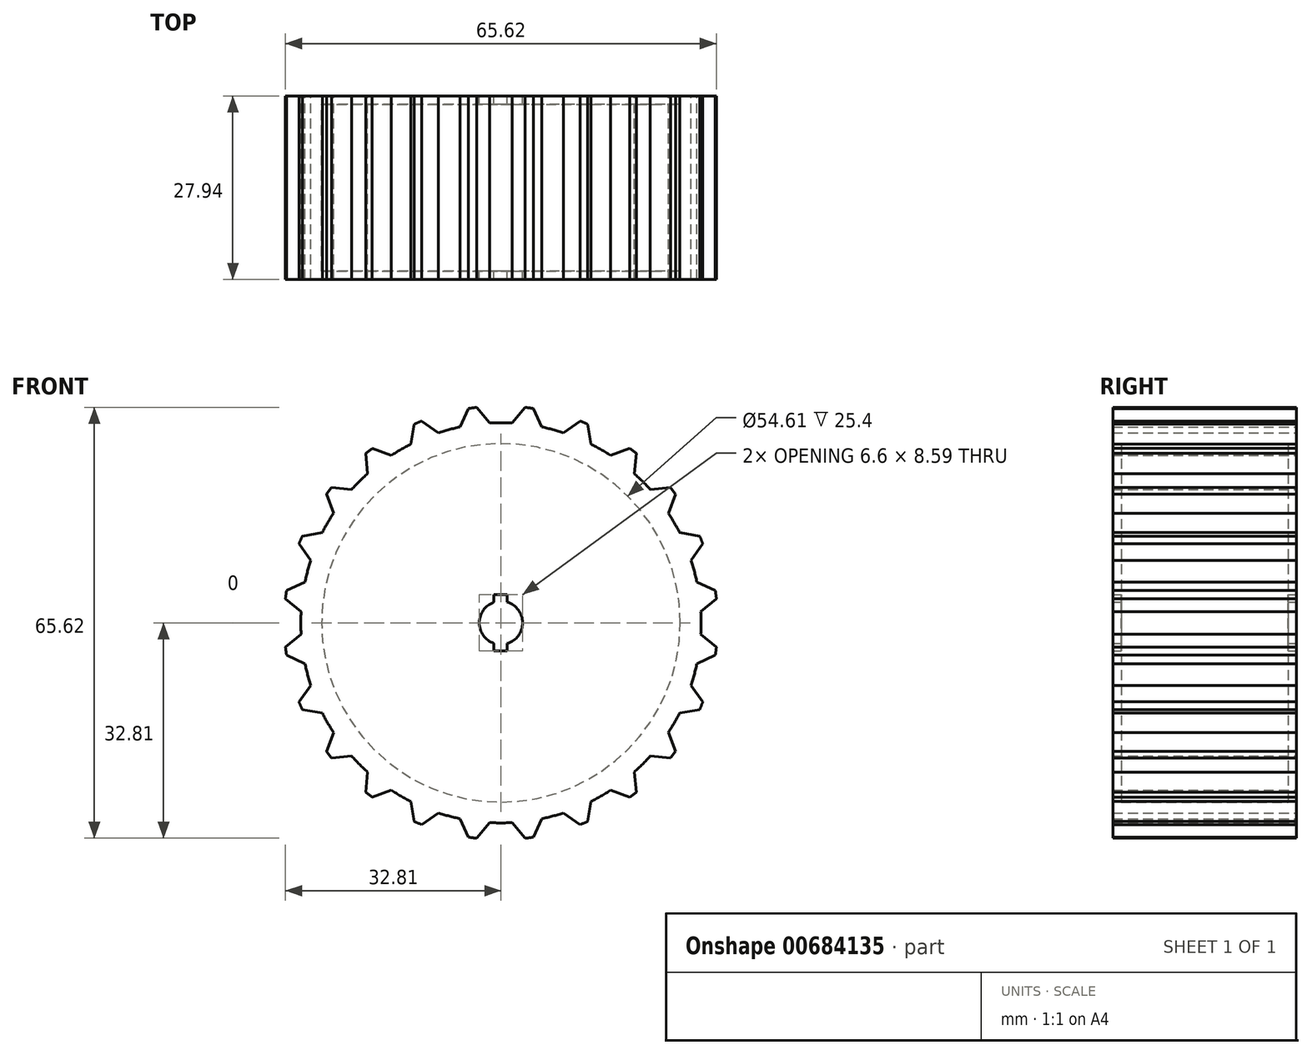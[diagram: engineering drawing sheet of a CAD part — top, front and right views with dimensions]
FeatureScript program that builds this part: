
annotation { "Feature Type Name" : "Feature", "Feature Type Description" : "" }
export const myFeature = defineFeature(function(context is Context, id is Id, definition is map)
    precondition{}
    {
        {
            var Q0;
            Q0=qCreatedBy(makeId("Front.planeOp"),FACE);
            var sketch = newSketch(context, id + "F0", { "sketchPlane" : qUnion([Q0])});
            skCircle(sketch, "E0", {"center": v(0, 0) * mm, "radius": 30.48 * mm});
            skCircle(sketch, "E1", {"center": v(0, 0) * mm, "radius": 33.02 * mm});
            skCircle(sketch, "E2.0", {"center": v(0, 0) * mm, "radius": 3.3 * mm});
            skLineSegment(sketch, "E3", {"start": v(-0.04, 5.09) * mm, "end": v(-0.04, -3.3) * mm, "construction": true});
            skLineSegment(sketch, "E4", {"start": v(-1.06, 3.13) * mm, "end": v(-1.06, 4.3) * mm});
            skLineSegment(sketch, "E5", {"start": v(-1.06, 4.3) * mm, "end": v(0.98, 4.3) * mm});
            skLineSegment(sketch, "E6", {"start": v(0.98, 4.3) * mm, "end": v(0.98, 3.15) * mm});
            skPoint(sketch, "E7", {"position": v(-0.04, 4.3) * mm});
            skLineSegment(sketch, "E8", {"start": v(0, 0) * mm, "end": v(-3.9, 0) * mm, "construction": true});
            skPoint(sketch, "E9.MirrorP", {"position": v(-0.04, -4.3) * mm});
            skLineSegment(sketch, "E10.MirrorCS", {"start": v(-1.06, -4.3) * mm, "end": v(0.98, -4.3) * mm});
            skLineSegment(sketch, "E11.MirrorCS", {"start": v(-1.06, -3.13) * mm, "end": v(-1.06, -4.3) * mm});
            skLineSegment(sketch, "E12.MirrorCS", {"start": v(0.98, -4.3) * mm, "end": v(0.98, -3.15) * mm});
            skSolve(sketch);
        }
        {
            var Q0;
            Q0 = qSketchRegion(id + "F0", true);
            extrude(context, id + "F1", {"entities" : qUnion([Q0]), "depth" : 27.94 * mm, "offsetDistance" : 25.4 * mm});
        }
        {
            var Q0;
            Q0=qCreatedBy(makeId("Front.planeOp"),FACE);
            var sketch = newSketch(context, id + "F2", { "sketchPlane" : qUnion([Q0])});
            skLineSegment(sketch, "E13", {"start": v(0, 44.27) * mm, "end": v(0, -42.94) * mm, "construction": true});
            skPoint(sketch, "E14", {"position": v(0, 33.02) * mm});
            skPoint(sketch, "E15", {"position": v(0, 30.48) * mm});
            skLineSegment(sketch, "E16", {"start": v(-1.71, 30.43) * mm, "end": v(-3.68, 32.81) * mm});
            skLineSegment(sketch, "E17", {"start": v(1.71, 30.43) * mm, "end": v(3.68, 32.81) * mm});
            skArc(sketch, "E18", {"start": v(3.68, 32.81) * mm, "mid": v(0, 33.02) * mm, "end": v(-3.68, 32.81) * mm});
            skArc(sketch, "E19", {"start": v(1.71, 30.43) * mm, "mid": v(0, 30.48) * mm, "end": v(-1.71, 30.43) * mm});
            skLineSegment(sketch, "E20.1.0", {"start": v(-6.22, 29.84) * mm, "end": v(-4.94, 32.65) * mm});
            skLineSegment(sketch, "E20.1.1", {"start": v(-9.53, 28.95) * mm, "end": v(-12.05, 30.74) * mm});
            skArc(sketch, "E20.1.2", {"start": v(-4.94, 32.65) * mm, "mid": v(-8.55, 31.9) * mm, "end": v(-12.05, 30.74) * mm});
            skArc(sketch, "E20.1.3", {"start": v(-6.22, 29.84) * mm, "mid": v(-7.89, 29.44) * mm, "end": v(-9.53, 28.95) * mm});
            skLineSegment(sketch, "E20.2.0", {"start": v(-13.73, 27.21) * mm, "end": v(-13.22, 30.26) * mm});
            skLineSegment(sketch, "E20.2.1", {"start": v(-16.7, 25.5) * mm, "end": v(-19.6, 26.58) * mm});
            skArc(sketch, "E20.2.2", {"start": v(-13.22, 30.26) * mm, "mid": v(-16.51, 28.6) * mm, "end": v(-19.6, 26.58) * mm});
            skArc(sketch, "E20.2.3", {"start": v(-13.73, 27.21) * mm, "mid": v(-15.24, 26.4) * mm, "end": v(-16.7, 25.5) * mm});
            skLineSegment(sketch, "E20.3.0", {"start": v(-20.3, 22.73) * mm, "end": v(-20.6, 25.8) * mm});
            skLineSegment(sketch, "E20.3.1", {"start": v(-22.73, 20.3) * mm, "end": v(-25.8, 20.6) * mm});
            skArc(sketch, "E20.3.2", {"start": v(-20.6, 25.8) * mm, "mid": v(-23.35, 23.35) * mm, "end": v(-25.8, 20.6) * mm});
            skArc(sketch, "E20.3.3", {"start": v(-20.3, 22.73) * mm, "mid": v(-21.55, 21.55) * mm, "end": v(-22.73, 20.3) * mm});
            skLineSegment(sketch, "E20.4.0", {"start": v(-25.5, 16.7) * mm, "end": v(-26.58, 19.6) * mm});
            skLineSegment(sketch, "E20.4.1", {"start": v(-27.21, 13.73) * mm, "end": v(-30.26, 13.22) * mm});
            skArc(sketch, "E20.4.2", {"start": v(-26.58, 19.6) * mm, "mid": v(-28.6, 16.5) * mm, "end": v(-30.26, 13.22) * mm});
            skArc(sketch, "E20.4.3", {"start": v(-25.5, 16.7) * mm, "mid": v(-26.4, 15.24) * mm, "end": v(-27.21, 13.73) * mm});
            skLineSegment(sketch, "E20.5.0", {"start": v(-28.95, 9.53) * mm, "end": v(-30.74, 12.05) * mm});
            skLineSegment(sketch, "E20.5.1", {"start": v(-29.84, 6.22) * mm, "end": v(-32.65, 4.94) * mm});
            skArc(sketch, "E20.5.2", {"start": v(-30.74, 12.05) * mm, "mid": v(-31.9, 8.55) * mm, "end": v(-32.65, 4.94) * mm});
            skArc(sketch, "E20.5.3", {"start": v(-28.95, 9.53) * mm, "mid": v(-29.44, 7.89) * mm, "end": v(-29.84, 6.22) * mm});
            skLineSegment(sketch, "E20.6.0", {"start": v(-30.43, 1.71) * mm, "end": v(-32.81, 3.68) * mm});
            skLineSegment(sketch, "E20.6.1", {"start": v(-30.43, -1.71) * mm, "end": v(-32.81, -3.68) * mm});
            skArc(sketch, "E20.6.2", {"start": v(-32.81, 3.68) * mm, "mid": v(-33.02, 0) * mm, "end": v(-32.81, -3.68) * mm});
            skArc(sketch, "E20.6.3", {"start": v(-30.43, 1.71) * mm, "mid": v(-30.48, 0) * mm, "end": v(-30.43, -1.71) * mm});
            skLineSegment(sketch, "E20.7.0", {"start": v(-29.84, -6.22) * mm, "end": v(-32.65, -4.94) * mm});
            skLineSegment(sketch, "E20.7.1", {"start": v(-28.95, -9.53) * mm, "end": v(-30.74, -12.05) * mm});
            skArc(sketch, "E20.7.2", {"start": v(-32.65, -4.94) * mm, "mid": v(-31.9, -8.55) * mm, "end": v(-30.74, -12.05) * mm});
            skArc(sketch, "E20.7.3", {"start": v(-29.84, -6.22) * mm, "mid": v(-29.44, -7.89) * mm, "end": v(-28.95, -9.53) * mm});
            skLineSegment(sketch, "E20.8.0", {"start": v(-27.21, -13.73) * mm, "end": v(-30.26, -13.22) * mm});
            skLineSegment(sketch, "E20.8.1", {"start": v(-25.5, -16.7) * mm, "end": v(-26.58, -19.6) * mm});
            skArc(sketch, "E20.8.2", {"start": v(-30.26, -13.22) * mm, "mid": v(-28.6, -16.5) * mm, "end": v(-26.58, -19.6) * mm});
            skArc(sketch, "E20.8.3", {"start": v(-27.21, -13.73) * mm, "mid": v(-26.4, -15.24) * mm, "end": v(-25.5, -16.7) * mm});
            skLineSegment(sketch, "E20.9.0", {"start": v(-22.73, -20.3) * mm, "end": v(-25.8, -20.6) * mm});
            skLineSegment(sketch, "E20.9.1", {"start": v(-20.3, -22.73) * mm, "end": v(-20.6, -25.8) * mm});
            skArc(sketch, "E20.9.2", {"start": v(-25.8, -20.6) * mm, "mid": v(-23.35, -23.35) * mm, "end": v(-20.6, -25.8) * mm});
            skArc(sketch, "E20.9.3", {"start": v(-22.73, -20.3) * mm, "mid": v(-21.55, -21.55) * mm, "end": v(-20.3, -22.73) * mm});
            skLineSegment(sketch, "E20.10.0", {"start": v(-16.7, -25.5) * mm, "end": v(-19.6, -26.58) * mm});
            skLineSegment(sketch, "E20.10.1", {"start": v(-13.73, -27.21) * mm, "end": v(-13.22, -30.26) * mm});
            skArc(sketch, "E20.10.2", {"start": v(-19.6, -26.58) * mm, "mid": v(-16.5, -28.6) * mm, "end": v(-13.22, -30.26) * mm});
            skArc(sketch, "E20.10.3", {"start": v(-16.7, -25.5) * mm, "mid": v(-15.24, -26.4) * mm, "end": v(-13.73, -27.21) * mm});
            skLineSegment(sketch, "E20.11.0", {"start": v(-9.53, -28.95) * mm, "end": v(-12.05, -30.74) * mm});
            skLineSegment(sketch, "E20.11.1", {"start": v(-6.22, -29.84) * mm, "end": v(-4.94, -32.65) * mm});
            skArc(sketch, "E20.11.2", {"start": v(-12.05, -30.74) * mm, "mid": v(-8.55, -31.9) * mm, "end": v(-4.94, -32.65) * mm});
            skArc(sketch, "E20.11.3", {"start": v(-9.53, -28.95) * mm, "mid": v(-7.89, -29.44) * mm, "end": v(-6.22, -29.84) * mm});
            skLineSegment(sketch, "E20.12.0", {"start": v(-1.71, -30.43) * mm, "end": v(-3.68, -32.81) * mm});
            skLineSegment(sketch, "E20.12.1", {"start": v(1.71, -30.43) * mm, "end": v(3.68, -32.81) * mm});
            skArc(sketch, "E20.12.2", {"start": v(-3.68, -32.81) * mm, "mid": v(0, -33.02) * mm, "end": v(3.68, -32.81) * mm});
            skArc(sketch, "E20.12.3", {"start": v(-1.71, -30.43) * mm, "mid": v(0, -30.48) * mm, "end": v(1.71, -30.43) * mm});
            skLineSegment(sketch, "E20.13.0", {"start": v(6.22, -29.84) * mm, "end": v(4.94, -32.65) * mm});
            skLineSegment(sketch, "E20.13.1", {"start": v(9.53, -28.95) * mm, "end": v(12.05, -30.74) * mm});
            skArc(sketch, "E20.13.2", {"start": v(4.94, -32.65) * mm, "mid": v(8.55, -31.9) * mm, "end": v(12.05, -30.74) * mm});
            skArc(sketch, "E20.13.3", {"start": v(6.22, -29.84) * mm, "mid": v(7.89, -29.44) * mm, "end": v(9.53, -28.95) * mm});
            skLineSegment(sketch, "E20.14.0", {"start": v(13.73, -27.21) * mm, "end": v(13.22, -30.26) * mm});
            skLineSegment(sketch, "E20.14.1", {"start": v(16.7, -25.5) * mm, "end": v(19.6, -26.58) * mm});
            skArc(sketch, "E20.14.2", {"start": v(13.22, -30.26) * mm, "mid": v(16.51, -28.6) * mm, "end": v(19.6, -26.58) * mm});
            skArc(sketch, "E20.14.3", {"start": v(13.73, -27.21) * mm, "mid": v(15.24, -26.4) * mm, "end": v(16.7, -25.5) * mm});
            skLineSegment(sketch, "E20.15.0", {"start": v(20.3, -22.73) * mm, "end": v(20.6, -25.8) * mm});
            skLineSegment(sketch, "E20.15.1", {"start": v(22.73, -20.3) * mm, "end": v(25.8, -20.6) * mm});
            skArc(sketch, "E20.15.2", {"start": v(20.6, -25.8) * mm, "mid": v(23.35, -23.35) * mm, "end": v(25.8, -20.6) * mm});
            skArc(sketch, "E20.15.3", {"start": v(20.3, -22.73) * mm, "mid": v(21.55, -21.55) * mm, "end": v(22.73, -20.3) * mm});
            skLineSegment(sketch, "E20.16.0", {"start": v(25.5, -16.7) * mm, "end": v(26.58, -19.6) * mm});
            skLineSegment(sketch, "E20.16.1", {"start": v(27.21, -13.73) * mm, "end": v(30.26, -13.22) * mm});
            skArc(sketch, "E20.16.2", {"start": v(26.58, -19.6) * mm, "mid": v(28.6, -16.5) * mm, "end": v(30.26, -13.22) * mm});
            skArc(sketch, "E20.16.3", {"start": v(25.5, -16.7) * mm, "mid": v(26.4, -15.24) * mm, "end": v(27.21, -13.73) * mm});
            skLineSegment(sketch, "E20.17.0", {"start": v(28.95, -9.53) * mm, "end": v(30.74, -12.05) * mm});
            skLineSegment(sketch, "E20.17.1", {"start": v(29.84, -6.22) * mm, "end": v(32.65, -4.94) * mm});
            skArc(sketch, "E20.17.2", {"start": v(30.74, -12.05) * mm, "mid": v(31.9, -8.55) * mm, "end": v(32.65, -4.94) * mm});
            skArc(sketch, "E20.17.3", {"start": v(28.95, -9.53) * mm, "mid": v(29.44, -7.89) * mm, "end": v(29.84, -6.22) * mm});
            skLineSegment(sketch, "E20.18.0", {"start": v(30.43, -1.71) * mm, "end": v(32.81, -3.68) * mm});
            skLineSegment(sketch, "E20.18.1", {"start": v(30.43, 1.71) * mm, "end": v(32.81, 3.68) * mm});
            skArc(sketch, "E20.18.2", {"start": v(32.81, -3.68) * mm, "mid": v(33.02, 0) * mm, "end": v(32.81, 3.68) * mm});
            skArc(sketch, "E20.18.3", {"start": v(30.43, -1.71) * mm, "mid": v(30.48, 0) * mm, "end": v(30.43, 1.71) * mm});
            skLineSegment(sketch, "E20.19.0", {"start": v(29.84, 6.22) * mm, "end": v(32.65, 4.94) * mm});
            skLineSegment(sketch, "E20.19.1", {"start": v(28.95, 9.53) * mm, "end": v(30.74, 12.05) * mm});
            skArc(sketch, "E20.19.2", {"start": v(32.65, 4.94) * mm, "mid": v(31.9, 8.55) * mm, "end": v(30.74, 12.05) * mm});
            skArc(sketch, "E20.19.3", {"start": v(29.84, 6.22) * mm, "mid": v(29.44, 7.89) * mm, "end": v(28.95, 9.53) * mm});
            skLineSegment(sketch, "E20.20.0", {"start": v(27.21, 13.73) * mm, "end": v(30.26, 13.22) * mm});
            skLineSegment(sketch, "E20.20.1", {"start": v(25.5, 16.7) * mm, "end": v(26.58, 19.6) * mm});
            skArc(sketch, "E20.20.2", {"start": v(30.26, 13.22) * mm, "mid": v(28.6, 16.51) * mm, "end": v(26.58, 19.6) * mm});
            skArc(sketch, "E20.20.3", {"start": v(27.21, 13.73) * mm, "mid": v(26.4, 15.24) * mm, "end": v(25.5, 16.7) * mm});
            skLineSegment(sketch, "E20.21.0", {"start": v(22.73, 20.3) * mm, "end": v(25.8, 20.6) * mm});
            skLineSegment(sketch, "E20.21.1", {"start": v(20.3, 22.73) * mm, "end": v(20.6, 25.8) * mm});
            skArc(sketch, "E20.21.2", {"start": v(25.8, 20.6) * mm, "mid": v(23.35, 23.35) * mm, "end": v(20.6, 25.8) * mm});
            skArc(sketch, "E20.21.3", {"start": v(22.73, 20.3) * mm, "mid": v(21.55, 21.55) * mm, "end": v(20.3, 22.73) * mm});
            skLineSegment(sketch, "E20.22.0", {"start": v(16.7, 25.5) * mm, "end": v(19.6, 26.58) * mm});
            skLineSegment(sketch, "E20.22.1", {"start": v(13.73, 27.21) * mm, "end": v(13.22, 30.26) * mm});
            skArc(sketch, "E20.22.2", {"start": v(19.6, 26.58) * mm, "mid": v(16.51, 28.6) * mm, "end": v(13.22, 30.26) * mm});
            skArc(sketch, "E20.22.3", {"start": v(16.7, 25.5) * mm, "mid": v(15.24, 26.4) * mm, "end": v(13.73, 27.21) * mm});
            skLineSegment(sketch, "E20.23.0", {"start": v(9.53, 28.95) * mm, "end": v(12.05, 30.74) * mm});
            skLineSegment(sketch, "E20.23.1", {"start": v(6.22, 29.84) * mm, "end": v(4.94, 32.65) * mm});
            skArc(sketch, "E20.23.2", {"start": v(12.05, 30.74) * mm, "mid": v(8.55, 31.9) * mm, "end": v(4.94, 32.65) * mm});
            skArc(sketch, "E20.23.3", {"start": v(9.53, 28.95) * mm, "mid": v(7.89, 29.44) * mm, "end": v(6.22, 29.84) * mm});
            skSolve(sketch);
        }
        {
            var Q0;
            Q0 = qSketchRegion(id + "F2", true);
            extrude(context, id + "F3", {"entities" : qUnion([Q0]), "operationType" : NewBodyOperationType.REMOVE, "depth" : 27.94 * mm, "offsetDistance" : 25.4 * mm});
        }
        {
            var Q0;
            Q0=makeQuery(id+"F0.imprint","IMPRINT",FACE,{"disambiguationData":[TD([[makeQuery(id+"F0.imprint","IMPRINT",EDGE,{"derivedFrom":sQuery(id+"F0.wireOp",EDGE,"E0")}),1.0]])]});
            extrude(context, id + "F4", {"entities" : qUnion([Q0]), "operationType" : NewBodyOperationType.ADD, "depth" : 27.94 * mm, "offsetDistance" : 25.4 * mm});
        }
        {
            var Q0;
            {var subQ0=sQuery(id+"F0.wireOp",EDGE,"E0");var subQ2=sQuery(id+"F0.wireOp",EDGE,"E1");var subQ4=makeQuery(id+"F1.opExtrude","CAP_FACE",FACE,{"disambiguationData":[OSD([subQ0,subQ2])],"isStart":true});Q0=makeQuery(id+"F4.boolean.opBoolean","MERGE",FACE,{"derivedFrom":[makeQuery(id+"F3.boolean.opBoolean","SPLIT",FACE,{"disambiguationData":[TD([makeQuery(id+"F3.opExtrude","SWEPT_FACE",FACE,{"disambiguationData":[OSD([sQuery(id+"F2.wireOp",EDGE,"E16")])]})])],"derivedFrom":subQ4}),makeQuery(id+"F3.boolean.opBoolean","SPLIT",FACE,{"disambiguationData":[TD([makeQuery(id+"F3.opExtrude","SWEPT_FACE",FACE,{"disambiguationData":[OSD([sQuery(id+"F2.wireOp",EDGE,"E17")])]})])],"derivedFrom":subQ4}),makeQuery(id+"F3.boolean.opBoolean","SPLIT",FACE,{"disambiguationData":[TD([makeQuery(id+"F3.opExtrude","SWEPT_FACE",FACE,{"disambiguationData":[OSD([sQuery(id+"F2.wireOp",EDGE,"E20.1.1")])]})])],"derivedFrom":subQ4}),makeQuery(id+"F3.boolean.opBoolean","SPLIT",FACE,{"disambiguationData":[TD([makeQuery(id+"F3.opExtrude","SWEPT_FACE",FACE,{"disambiguationData":[OSD([sQuery(id+"F2.wireOp",EDGE,"E20.2.1")])]})])],"derivedFrom":subQ4}),makeQuery(id+"F3.boolean.opBoolean","SPLIT",FACE,{"disambiguationData":[TD([makeQuery(id+"F3.opExtrude","SWEPT_FACE",FACE,{"disambiguationData":[OSD([sQuery(id+"F2.wireOp",EDGE,"E20.3.1")])]})])],"derivedFrom":subQ4}),makeQuery(id+"F3.boolean.opBoolean","SPLIT",FACE,{"disambiguationData":[TD([makeQuery(id+"F3.opExtrude","SWEPT_FACE",FACE,{"disambiguationData":[OSD([sQuery(id+"F2.wireOp",EDGE,"E20.4.1")])]})])],"derivedFrom":subQ4}),makeQuery(id+"F3.boolean.opBoolean","SPLIT",FACE,{"disambiguationData":[TD([makeQuery(id+"F3.opExtrude","SWEPT_FACE",FACE,{"disambiguationData":[OSD([sQuery(id+"F2.wireOp",EDGE,"E20.5.1")])]})])],"derivedFrom":subQ4}),makeQuery(id+"F3.boolean.opBoolean","SPLIT",FACE,{"disambiguationData":[TD([makeQuery(id+"F3.opExtrude","SWEPT_FACE",FACE,{"disambiguationData":[OSD([sQuery(id+"F2.wireOp",EDGE,"E20.6.1")])]})])],"derivedFrom":subQ4}),makeQuery(id+"F3.boolean.opBoolean","SPLIT",FACE,{"disambiguationData":[TD([makeQuery(id+"F3.opExtrude","SWEPT_FACE",FACE,{"disambiguationData":[OSD([sQuery(id+"F2.wireOp",EDGE,"E20.7.1")])]})])],"derivedFrom":subQ4}),makeQuery(id+"F3.boolean.opBoolean","SPLIT",FACE,{"disambiguationData":[TD([makeQuery(id+"F3.opExtrude","SWEPT_FACE",FACE,{"disambiguationData":[OSD([sQuery(id+"F2.wireOp",EDGE,"E20.8.1")])]})])],"derivedFrom":subQ4}),makeQuery(id+"F3.boolean.opBoolean","SPLIT",FACE,{"disambiguationData":[TD([makeQuery(id+"F3.opExtrude","SWEPT_FACE",FACE,{"disambiguationData":[OSD([sQuery(id+"F2.wireOp",EDGE,"E20.9.1")])]})])],"derivedFrom":subQ4}),makeQuery(id+"F3.boolean.opBoolean","SPLIT",FACE,{"disambiguationData":[TD([makeQuery(id+"F3.opExtrude","SWEPT_FACE",FACE,{"disambiguationData":[OSD([sQuery(id+"F2.wireOp",EDGE,"E20.10.1")])]})])],"derivedFrom":subQ4}),makeQuery(id+"F3.boolean.opBoolean","SPLIT",FACE,{"disambiguationData":[TD([makeQuery(id+"F3.opExtrude","SWEPT_FACE",FACE,{"disambiguationData":[OSD([sQuery(id+"F2.wireOp",EDGE,"E20.11.1")])]})])],"derivedFrom":subQ4}),makeQuery(id+"F3.boolean.opBoolean","SPLIT",FACE,{"disambiguationData":[TD([makeQuery(id+"F3.opExtrude","SWEPT_FACE",FACE,{"disambiguationData":[OSD([sQuery(id+"F2.wireOp",EDGE,"E20.12.1")])]})])],"derivedFrom":subQ4}),makeQuery(id+"F3.boolean.opBoolean","SPLIT",FACE,{"disambiguationData":[TD([makeQuery(id+"F3.opExtrude","SWEPT_FACE",FACE,{"disambiguationData":[OSD([sQuery(id+"F2.wireOp",EDGE,"E20.13.1")])]})])],"derivedFrom":subQ4}),makeQuery(id+"F3.boolean.opBoolean","SPLIT",FACE,{"disambiguationData":[TD([makeQuery(id+"F3.opExtrude","SWEPT_FACE",FACE,{"disambiguationData":[OSD([sQuery(id+"F2.wireOp",EDGE,"E20.14.1")])]})])],"derivedFrom":subQ4}),makeQuery(id+"F3.boolean.opBoolean","SPLIT",FACE,{"disambiguationData":[TD([makeQuery(id+"F3.opExtrude","SWEPT_FACE",FACE,{"disambiguationData":[OSD([sQuery(id+"F2.wireOp",EDGE,"E20.15.1")])]})])],"derivedFrom":subQ4}),makeQuery(id+"F3.boolean.opBoolean","SPLIT",FACE,{"disambiguationData":[TD([makeQuery(id+"F3.opExtrude","SWEPT_FACE",FACE,{"disambiguationData":[OSD([sQuery(id+"F2.wireOp",EDGE,"E20.16.1")])]})])],"derivedFrom":subQ4}),makeQuery(id+"F3.boolean.opBoolean","SPLIT",FACE,{"disambiguationData":[TD([makeQuery(id+"F3.opExtrude","SWEPT_FACE",FACE,{"disambiguationData":[OSD([sQuery(id+"F2.wireOp",EDGE,"E20.17.1")])]})])],"derivedFrom":subQ4}),makeQuery(id+"F3.boolean.opBoolean","SPLIT",FACE,{"disambiguationData":[TD([makeQuery(id+"F3.opExtrude","SWEPT_FACE",FACE,{"disambiguationData":[OSD([sQuery(id+"F2.wireOp",EDGE,"E20.18.1")])]})])],"derivedFrom":subQ4}),makeQuery(id+"F3.boolean.opBoolean","SPLIT",FACE,{"disambiguationData":[TD([makeQuery(id+"F3.opExtrude","SWEPT_FACE",FACE,{"disambiguationData":[OSD([sQuery(id+"F2.wireOp",EDGE,"E20.19.1")])]})])],"derivedFrom":subQ4}),makeQuery(id+"F3.boolean.opBoolean","SPLIT",FACE,{"disambiguationData":[TD([makeQuery(id+"F3.opExtrude","SWEPT_FACE",FACE,{"disambiguationData":[OSD([sQuery(id+"F2.wireOp",EDGE,"E20.20.1")])]})])],"derivedFrom":subQ4}),makeQuery(id+"F3.boolean.opBoolean","SPLIT",FACE,{"disambiguationData":[TD([makeQuery(id+"F3.opExtrude","SWEPT_FACE",FACE,{"disambiguationData":[OSD([sQuery(id+"F2.wireOp",EDGE,"E20.21.1")])]})])],"derivedFrom":subQ4}),makeQuery(id+"F3.boolean.opBoolean","SPLIT",FACE,{"disambiguationData":[TD([makeQuery(id+"F3.opExtrude","SWEPT_FACE",FACE,{"disambiguationData":[OSD([sQuery(id+"F2.wireOp",EDGE,"E20.22.1")])]})])],"derivedFrom":subQ4}),makeQuery(id+"F4.opExtrude","CAP_FACE",FACE,{"disambiguationData":[OSD([subQ0,sQuery(id+"F0.wireOp",EDGE,"E2.0"),sQuery(id+"F0.wireOp",EDGE,"E4"),sQuery(id+"F0.wireOp",EDGE,"E5"),sQuery(id+"F0.wireOp",EDGE,"E6"),sQuery(id+"F0.wireOp",EDGE,"c42b0e2f-e0df-4360-b1c6-a7395f8d7f6a.MirrorCS"),sQuery(id+"F0.wireOp",EDGE,"372de0da-1b8b-46dc-9e8a-f7d76659ff2b.MirrorCS"),sQuery(id+"F0.wireOp",EDGE,"2b10c652-e143-4620-85a8-c68cb282d4e6.MirrorCS")])],"isStart":true})]});}
            cPlane(context, id + "F5", {"entities" : qUnion([Q0]), "cplaneType" : CPlaneType.OFFSET, "offset" : 1.27 * mm, "oppositeDirection" : true, "width" : 152.4 * mm, "height" : 152.4 * mm});
        }
        {
            var Q0;
            Q0=qCreatedBy(id+"F5.planeOp",FACE);
            var sketch = newSketch(context, id + "F6", { "sketchPlane" : qUnion([Q0])});
            skCircle(sketch, "E21.0", {"center": v(0, 0) * mm, "radius": 27.3 * mm});
            skSolve(sketch);
        }
        {
            var Q0;
            Q0 = qSketchRegion(id + "F6", true);
            var Q1;
            Q1=sQuery(id+"F6.wireOp",EDGE,"E21.0");
            extrude(context, id + "F7", {"entities" : qUnion([Q0]), "operationType" : NewBodyOperationType.REMOVE, "surfaceEntities" : qUnion([Q1]), "oppositeDirection" : true, "depth" : 25.4 * mm, "offsetDistance" : 25.4 * mm});
        }
    });
